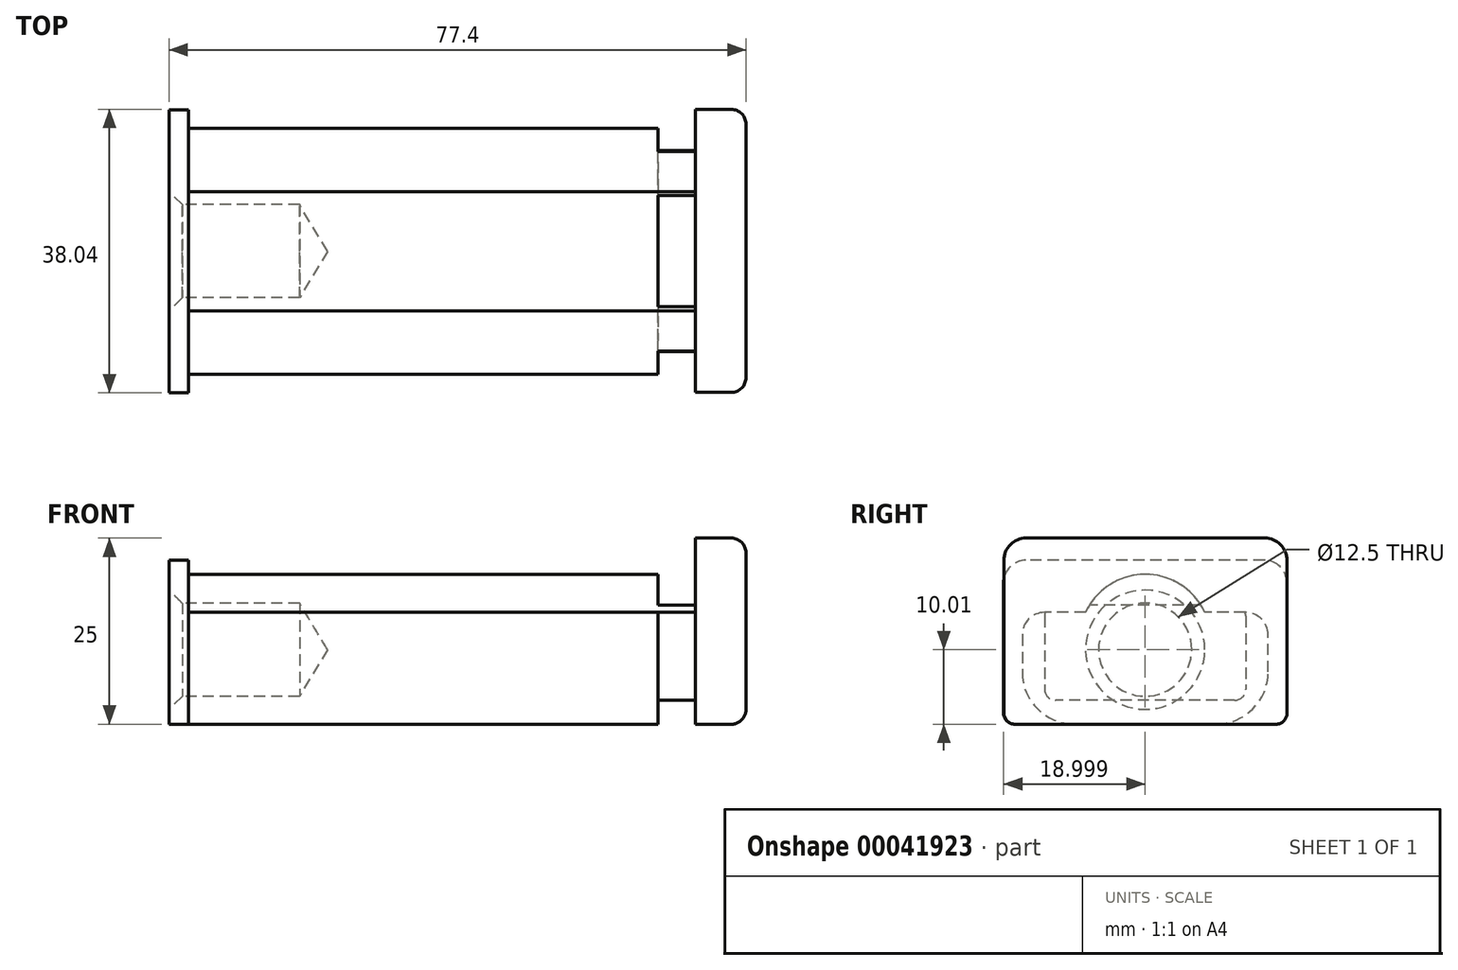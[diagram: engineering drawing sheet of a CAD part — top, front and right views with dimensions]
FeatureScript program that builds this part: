
annotation { "Feature Type Name" : "Feature", "Feature Type Description" : "" }
export const myFeature = defineFeature(function(context is Context, id is Id, definition is map)
    precondition{}
    {
        {
            var Q0;
            Q0=qCreatedBy(makeId("Right.planeOp"),FACE);
            var sketch = newSketch(context, id + "F0", { "sketchPlane" : qUnion([Q0])});
            skLineSegment(sketch, "E0", {"start": v(-14.88, 5.77) * mm, "end": v(-14.88, -11.73) * mm});
            skLineSegment(sketch, "E1", {"start": v(-13.38, -13.23) * mm, "end": v(21.62, -13.23) * mm});
            skLineSegment(sketch, "E2", {"start": v(23.12, -11.73) * mm, "end": v(23.12, 5.77) * mm});
            skLineSegment(sketch, "E3", {"start": v(20.12, 8.77) * mm, "end": v(-11.88, 8.77) * mm});
            skPoint(sketch, "E4.visualSharp", {"position": v(-14.88, 8.77) * mm});
            skArc(sketch, "E4.filletArc", {"start": v(-11.88, 8.77) * mm, "mid": v(-14, 7.9) * mm, "end": v(-14.88, 5.77) * mm});
            skPoint(sketch, "E5.visualSharp", {"position": v(23.12, 8.77) * mm});
            skArc(sketch, "E5.filletArc", {"start": v(23.12, 5.77) * mm, "mid": v(22.24, 7.9) * mm, "end": v(20.12, 8.77) * mm});
            skPoint(sketch, "E6.visualSharp", {"position": v(-14.88, -13.23) * mm});
            skArc(sketch, "E6.filletArc", {"start": v(-14.88, -11.73) * mm, "mid": v(-14.44, -12.8) * mm, "end": v(-13.38, -13.23) * mm});
            skPoint(sketch, "E7.visualSharp", {"position": v(23.12, -13.23) * mm});
            skArc(sketch, "E7.filletArc", {"start": v(21.62, -13.23) * mm, "mid": v(22.68, -12.8) * mm, "end": v(23.12, -11.73) * mm});
            skSolve(sketch);
        }
        {
            var Q0;
            Q0=makeQuery(id+"F0.imprint","IMPRINT",FACE,{"disambiguationData":[TD([[makeQuery(id+"F0.imprint","IMPRINT",EDGE,{"derivedFrom":sQuery(id+"F0.wireOp",EDGE,"E0")}),1.0]])]});
            extrude(context, id + "F1", {"entities" : qUnion([Q0]), "depth" : 2.6 * mm});
        }
        {
            var Q0;
            Q0=makeQuery(id+"F1.opExtrude","CAP_FACE",FACE,{"disambiguationData":[OSD([sQuery(id+"F0.wireOp",EDGE,"E0"),sQuery(id+"F0.wireOp",EDGE,"E1"),sQuery(id+"F0.wireOp",EDGE,"E2"),sQuery(id+"F0.wireOp",EDGE,"E3"),sQuery(id+"F0.wireOp",EDGE,"E4.filletArc"),sQuery(id+"F0.wireOp",EDGE,"E5.filletArc"),sQuery(id+"F0.wireOp",EDGE,"E6.filletArc"),sQuery(id+"F0.wireOp",EDGE,"E7.filletArc")])],"isStart":false});
            var sketch = newSketch(context, id + "F2", { "sketchPlane" : qUnion([Q0])});
            skPoint(sketch, "E8", {"position": v(4.12, -13.23) * mm});
            skLineSegment(sketch, "E9", {"start": v(4.12, -13.23) * mm, "end": v(13.62, -13.23) * mm});
            skLineSegment(sketch, "E10", {"start": v(20.62, -6.23) * mm, "end": v(20.62, -1.23) * mm});
            skLineSegment(sketch, "E11", {"start": v(17.62, 1.77) * mm, "end": v(12.12, 1.77) * mm});
            skLineSegment(sketch, "E12", {"start": v(-12.38, -1.23) * mm, "end": v(-12.38, -6.23) * mm});
            skLineSegment(sketch, "E13", {"start": v(-5.38, -13.23) * mm, "end": v(4.12, -13.23) * mm});
            skPoint(sketch, "E14.visualSharp", {"position": v(20.62, 1.77) * mm});
            skArc(sketch, "E14.filletArc", {"start": v(20.62, -1.23) * mm, "mid": v(19.74, 0.9) * mm, "end": v(17.62, 1.77) * mm});
            skPoint(sketch, "E15.visualSharp", {"position": v(-12.38, 1.77) * mm});
            skArc(sketch, "E15.filletArc", {"start": v(-9.38, 1.77) * mm, "mid": v(-11.5, 0.9) * mm, "end": v(-12.38, -1.23) * mm});
            skLineSegment(sketch, "E16.trimOffspring", {"start": v(-3.88, 1.77) * mm, "end": v(-9.38, 1.77) * mm});
            skArc(sketch, "E17", {"start": v(12.12, 1.77) * mm, "mid": v(4.12, 6.88) * mm, "end": v(-3.88, 1.77) * mm});
            skPoint(sketch, "E18.visualSharp", {"position": v(-12.38, -13.23) * mm});
            skArc(sketch, "E18.filletArc", {"start": v(-12.38, -6.23) * mm, "mid": v(-10.33, -11.18) * mm, "end": v(-5.38, -13.23) * mm});
            skPoint(sketch, "E19.visualSharp", {"position": v(20.62, -13.23) * mm});
            skArc(sketch, "E19.filletArc", {"start": v(13.62, -13.23) * mm, "mid": v(18.57, -11.18) * mm, "end": v(20.62, -6.23) * mm});
            skSolve(sketch);
        }
        {
            var Q0;
            Q0=makeQuery(id+"F2.imprint","IMPRINT",FACE,{"disambiguationData":[TD([[makeQuery(id+"F2.imprint","IMPRINT",EDGE,{"derivedFrom":sQuery(id+"F2.wireOp",EDGE,"E9")}),1.0]])]});
            extrude(context, id + "F3", {"entities" : qUnion([Q0]), "operationType" : NewBodyOperationType.ADD, "depth" : 60 * mm});
        }
        {
            var Q0;
            Q0=makeQuery(id+"F3.opExtrude","CAP_FACE",FACE,{"disambiguationData":[OSD([sQuery(id+"F2.wireOp",EDGE,"E9"),sQuery(id+"F2.wireOp",EDGE,"E10"),sQuery(id+"F2.wireOp",EDGE,"E11"),sQuery(id+"F2.wireOp",EDGE,"E12"),sQuery(id+"F2.wireOp",EDGE,"E13"),sQuery(id+"F2.wireOp",EDGE,"E14.filletArc"),sQuery(id+"F2.wireOp",EDGE,"E15.filletArc"),sQuery(id+"F2.wireOp",EDGE,"22844c3f-7400-4db0-826f-0b4cdc1ca621"),sQuery(id+"F2.wireOp",EDGE,"E16.trimOffspring")])],"isStart":false});
            var sketch = newSketch(context, id + "F4", { "sketchPlane" : qUnion([Q0])});
            skArc(sketch, "E20.0.0", {"start": v(-14.88, 5.77) * mm, "mid": v(-14, 7.9) * mm, "end": v(-11.88, 8.77) * mm});
            skLineSegment(sketch, "E20.0.1", {"start": v(-11.88, 8.77) * mm, "end": v(20.12, 8.77) * mm});
            skArc(sketch, "E20.0.2", {"start": v(20.12, 8.77) * mm, "mid": v(22.24, 7.9) * mm, "end": v(23.12, 5.77) * mm});
            skLineSegment(sketch, "E20.0.3", {"start": v(23.12, 5.77) * mm, "end": v(23.12, -11.73) * mm});
            skArc(sketch, "E20.0.4", {"start": v(23.12, -11.73) * mm, "mid": v(22.68, -12.8) * mm, "end": v(21.62, -13.23) * mm});
            skLineSegment(sketch, "E20.0.5", {"start": v(21.62, -13.23) * mm, "end": v(-13.38, -13.23) * mm});
            skArc(sketch, "E20.0.6", {"start": v(-13.38, -13.23) * mm, "mid": v(-14.44, -12.8) * mm, "end": v(-14.88, -11.73) * mm});
            skLineSegment(sketch, "E20.0.7", {"start": v(-14.88, -11.73) * mm, "end": v(-14.88, 5.77) * mm});
            skSolve(sketch);
        }
        {
            var Q0;
            Q0=makeQuery(id+"F4.imprint","IMPRINT",FACE,{"disambiguationData":[TD([[makeQuery(id+"F4.imprint","IMPRINT",EDGE,{"derivedFrom":sQuery(id+"F4.wireOp",EDGE,"E20.0.0")}),-1.0]])]});
            var Q1;
            {var subQ2=makeQuery(id+"F3.opExtrude","CAP_EDGE",EDGE,{"disambiguationData":[OSD([sQuery(id+"F2.wireOp",EDGE,"E10")])],"isStart":false});Q1=makeQuery(id+"F4.imprint","IMPRINT",FACE,{"disambiguationData":[TD([[makeQuery(id+"F4.imprint","IMPRINT",EDGE,{"derivedFrom":subQ2}),1.0]])]});}
            extrude(context, id + "F5", {"entities" : qUnion([Q0, Q1]), "operationType" : NewBodyOperationType.ADD, "depth" : 3 * mm});
        }
        {
            var Q0;
            Q0=makeQuery(id+"F1.opExtrude","CAP_FACE",FACE,{"disambiguationData":[OSD([sQuery(id+"F0.wireOp",EDGE,"E0"),sQuery(id+"F0.wireOp",EDGE,"E1"),sQuery(id+"F0.wireOp",EDGE,"E2"),sQuery(id+"F0.wireOp",EDGE,"E3"),sQuery(id+"F0.wireOp",EDGE,"E4.filletArc"),sQuery(id+"F0.wireOp",EDGE,"E5.filletArc"),sQuery(id+"F0.wireOp",EDGE,"E6.filletArc"),sQuery(id+"F0.wireOp",EDGE,"E7.filletArc")])],"isStart":true});
            var sketch = newSketch(context, id + "F6", { "sketchPlane" : qUnion([Q0])});
            skPoint(sketch, "E21", {"position": v(-4.12, 8.77) * mm});
            skPoint(sketch, "E22", {"position": v(-23.12, -2.98) * mm});
            skCircle(sketch, "E23", {"center": v(-4.12, -3.23) * mm, "radius": 5.5 * mm});
            skSolve(sketch);
        }
        {
            var Q0;
            Q0=sQuery(id+"F6.wireOp",VERTEX,"E23.center");
            var Q1;
            Q1=makeQuery(id+"F1.opExtrude","SWEPT_BODY",BODY,{"disambiguationData":[OSD([sQuery(id+"F0.wireOp",EDGE,"E0"),sQuery(id+"F0.wireOp",EDGE,"E1"),sQuery(id+"F0.wireOp",EDGE,"E2"),sQuery(id+"F0.wireOp",EDGE,"E3"),sQuery(id+"F0.wireOp",EDGE,"E4.filletArc"),sQuery(id+"F0.wireOp",EDGE,"E5.filletArc"),sQuery(id+"F0.wireOp",EDGE,"E6.filletArc"),sQuery(id+"F0.wireOp",EDGE,"E7.filletArc")])]});
            hole(context, id + "F7", {"style" : HoleStyle.C_SINK, "holeDiameter" : 12.5 * mm, "cSinkDiameter" : 16 * mm, "endStyle" : HoleEndStyle.BLIND, "holeDepth" : 17.5 * mm, "locations" : qUnion([Q0]), "scope" : qUnion([Q1]), "cSinkAngle" : 90 * degree});
        }
        {
            var Q0;
            Q0=makeQuery(id+"F5.opExtrude","CAP_FACE",FACE,{"disambiguationData":[OSD([sQuery(id+"F4.wireOp",EDGE,"E20.0.0"),sQuery(id+"F4.wireOp",EDGE,"E20.0.1"),sQuery(id+"F4.wireOp",EDGE,"E20.0.2"),sQuery(id+"F4.wireOp",EDGE,"E20.0.3"),sQuery(id+"F4.wireOp",EDGE,"E20.0.4"),sQuery(id+"F4.wireOp",EDGE,"E20.0.5"),sQuery(id+"F4.wireOp",EDGE,"E20.0.6"),sQuery(id+"F4.wireOp",EDGE,"E20.0.7")])],"isStart":false});
            var sketch = newSketch(context, id + "F8", { "sketchPlane" : qUnion([Q0])});
            skLineSegment(sketch, "E24", {"start": v(4.12, 8.77) * mm, "end": v(4.12, 2.77) * mm});
            skLineSegment(sketch, "E25", {"start": v(4.12, -13.23) * mm, "end": v(4.12, -10.03) * mm});
            skLineSegment(sketch, "E26.rect.bottom", {"start": v(16.12, 2.77) * mm, "end": v(-7.88, 2.77) * mm});
            skLineSegment(sketch, "E26.rect.top", {"start": v(16.12, -10.03) * mm, "end": v(-7.88, -10.03) * mm});
            skLineSegment(sketch, "E26.rect.left", {"start": v(17.62, 1.27) * mm, "end": v(17.62, -8.53) * mm});
            skLineSegment(sketch, "E26.rect.right", {"start": v(-9.38, 1.27) * mm, "end": v(-9.38, -8.53) * mm});
            skPoint(sketch, "E26.rect.middle", {"position": v(4.12, -3.63) * mm});
            skPoint(sketch, "E27.visualSharp", {"position": v(-9.38, 2.77) * mm});
            skArc(sketch, "E27.filletArc", {"start": v(-7.88, 2.77) * mm, "mid": v(-8.94, 2.33) * mm, "end": v(-9.38, 1.27) * mm});
            skPoint(sketch, "E28.visualSharp", {"position": v(17.62, 2.77) * mm});
            skArc(sketch, "E28.filletArc", {"start": v(17.62, 1.27) * mm, "mid": v(17.18, 2.33) * mm, "end": v(16.12, 2.77) * mm});
            skPoint(sketch, "E29.visualSharp", {"position": v(17.62, -10.03) * mm});
            skArc(sketch, "E29.filletArc", {"start": v(16.12, -10.03) * mm, "mid": v(17.18, -9.6) * mm, "end": v(17.62, -8.53) * mm});
            skPoint(sketch, "E30.visualSharp", {"position": v(-9.38, -10.03) * mm});
            skArc(sketch, "E30.filletArc", {"start": v(-9.38, -8.53) * mm, "mid": v(-8.94, -9.6) * mm, "end": v(-7.88, -10.03) * mm});
            skSolve(sketch);
        }
        {
            var Q0;
            Q0=makeQuery(id+"F8.imprint","IMPRINT",FACE,{"disambiguationData":[TD([[makeQuery(id+"F8.imprint","IMPRINT",EDGE,{"derivedFrom":sQuery(id+"F8.wireOp",EDGE,"E26.rect.left")}),-1.0]])]});
            extrude(context, id + "F9", {"entities" : qUnion([Q0]), "operationType" : NewBodyOperationType.ADD, "depth" : 5 * mm});
        }
        {
            var Q0;
            Q0=makeQuery(id+"F9.opExtrude","CAP_FACE",FACE,{"disambiguationData":[OSD([sQuery(id+"F8.wireOp",EDGE,"E26.rect.bottom"),sQuery(id+"F8.wireOp",EDGE,"E26.rect.top"),sQuery(id+"F8.wireOp",EDGE,"E26.rect.left"),sQuery(id+"F8.wireOp",EDGE,"E26.rect.right"),sQuery(id+"F8.wireOp",EDGE,"E27.filletArc"),sQuery(id+"F8.wireOp",EDGE,"E28.filletArc"),sQuery(id+"F8.wireOp",EDGE,"E29.filletArc"),sQuery(id+"F8.wireOp",EDGE,"E30.filletArc")])],"isStart":false});
            var sketch = newSketch(context, id + "F10", { "sketchPlane" : qUnion([Q0])});
            skLineSegment(sketch, "E31", {"start": v(-14.84, 8.76) * mm, "end": v(-14.84, -11.74) * mm});
            skLineSegment(sketch, "E32", {"start": v(-13.34, -13.24) * mm, "end": v(21.66, -13.24) * mm});
            skLineSegment(sketch, "E33", {"start": v(23.16, -11.74) * mm, "end": v(23.16, 8.76) * mm});
            skLineSegment(sketch, "E34", {"start": v(20.16, 11.76) * mm, "end": v(-11.84, 11.76) * mm});
            skPoint(sketch, "E35.visualSharp", {"position": v(-14.84, 11.76) * mm});
            skArc(sketch, "E35.filletArc", {"start": v(-11.84, 11.76) * mm, "mid": v(-13.96, 10.88) * mm, "end": v(-14.84, 8.76) * mm});
            skPoint(sketch, "E36.visualSharp", {"position": v(23.16, 11.76) * mm});
            skArc(sketch, "E36.filletArc", {"start": v(23.16, 8.76) * mm, "mid": v(22.28, 10.88) * mm, "end": v(20.16, 11.76) * mm});
            skPoint(sketch, "E37.visualSharp", {"position": v(-14.84, -13.24) * mm});
            skArc(sketch, "E37.filletArc", {"start": v(-14.84, -11.74) * mm, "mid": v(-14.4, -12.8) * mm, "end": v(-13.34, -13.24) * mm});
            skPoint(sketch, "E38.visualSharp", {"position": v(23.16, -13.24) * mm});
            skArc(sketch, "E38.filletArc", {"start": v(21.66, -13.24) * mm, "mid": v(22.72, -12.8) * mm, "end": v(23.16, -11.74) * mm});
            skSolve(sketch);
        }
        {
            var Q0;
            Q0=makeQuery(id+"F10.imprint","IMPRINT",FACE,{"disambiguationData":[TD([[makeQuery(id+"F10.imprint","IMPRINT",EDGE,{"derivedFrom":sQuery(id+"F10.wireOp",EDGE,"E31")}),1.0]])]});
            var Q1;
            Q1=makeQuery(id+"F10.imprint","IMPRINT",FACE,{"disambiguationData":[TD([[makeQuery(id+"F10.imprint","IMPRINT",EDGE,{"derivedFrom":makeQuery(id+"F9.opExtrude","CAP_EDGE",EDGE,{"disambiguationData":[OSD([sQuery(id+"F8.wireOp",EDGE,"E26.rect.bottom")])],"isStart":false})}),1.0]])]});
            extrude(context, id + "F11", {"entities" : qUnion([Q0, Q1]), "operationType" : NewBodyOperationType.ADD, "depth" : 6.8 * mm});
        }
        {
            var Q0;
            Q0=makeQuery(id+"F11.opExtrude","CAP_FACE",FACE,{"disambiguationData":[OSD([sQuery(id+"F10.wireOp",EDGE,"E31"),sQuery(id+"F10.wireOp",EDGE,"E32"),sQuery(id+"F10.wireOp",EDGE,"E33"),sQuery(id+"F10.wireOp",EDGE,"E34"),sQuery(id+"F10.wireOp",EDGE,"E35.filletArc"),sQuery(id+"F10.wireOp",EDGE,"E36.filletArc"),sQuery(id+"F10.wireOp",EDGE,"E37.filletArc"),sQuery(id+"F10.wireOp",EDGE,"E38.filletArc")])],"isStart":false});
            fillet(context, id + "F12", {"entities" : qUnion([Q0]), "radius" : 2 * mm, "tangentPropagation" : true, "allowEdgeOverflow" : false});
        }
    });
